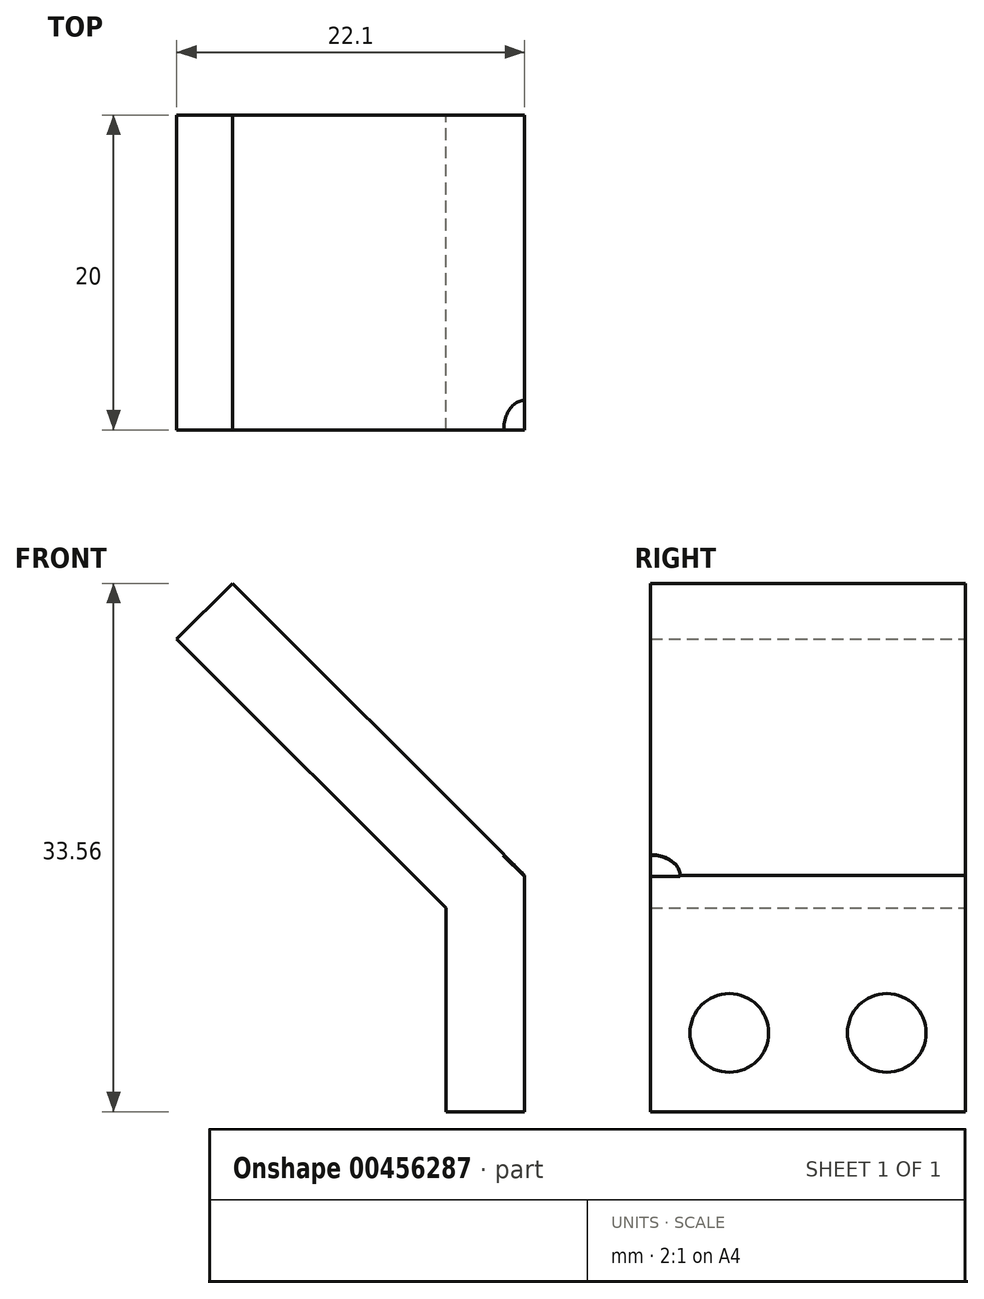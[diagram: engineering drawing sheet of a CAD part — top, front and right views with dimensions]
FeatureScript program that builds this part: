
annotation { "Feature Type Name" : "Feature", "Feature Type Description" : "" }
export const myFeature = defineFeature(function(context is Context, id is Id, definition is map)
    precondition{}
    {
        {
            var Q0;
            Q0=qCreatedBy(makeId("Front.planeOp"),FACE);
            var sketch = newSketch(context, id + "F0", { "sketchPlane" : qUnion([Q0])});
            skLineSegment(sketch, "E0", {"start": v(0, 0) * mm, "end": v(0, -15) * mm});
            skLineSegment(sketch, "E1", {"start": v(0, -15) * mm, "end": v(-5, -15) * mm});
            skLineSegment(sketch, "E2", {"start": v(-5, -15) * mm, "end": v(-5, -2.07) * mm});
            skLineSegment(sketch, "E3", {"start": v(-5, -2.07) * mm, "end": v(-22.1, 15.03) * mm});
            skLineSegment(sketch, "E4", {"start": v(-22.1, 15.03) * mm, "end": v(-18.56, 18.56) * mm});
            skLineSegment(sketch, "E5", {"start": v(-18.56, 18.56) * mm, "end": v(0, 0) * mm});
            skLineSegment(sketch, "E6", {"start": v(0, 0) * mm, "end": v(-5, -2.07) * mm});
            skSolve(sketch);
        }
        {
            var Q0;
            Q0 = qSketchRegion(id + "F0", true);
            extrude(context, id + "F1", {"entities" : qUnion([Q0]), "endBound" : BoundingType.SYMMETRIC, "depth" : 20 * mm, "offsetDistance" : 25 * mm});
        }
        {
            var Q0;
            Q0=makeQuery(id+"F1.opExtrude","SWEPT_FACE",FACE,{"disambiguationData":[OSD([sQuery(id+"F0.wireOp",EDGE,"E5")])]});
            var sketch = newSketch(context, id + "F2", { "sketchPlane" : qUnion([Q0])});
            skLineSegment(sketch, "E7", {"start": v(-26.25, 0) * mm, "end": v(-26.25, -6.25) * mm});
            skLineSegment(sketch, "E8", {"start": v(-26.25, 0) * mm, "end": v(-26.25, 6.25) * mm});
            skLineSegment(sketch, "E9", {"start": v(-26.25, 6.25) * mm, "end": v(0, 10) * mm});
            skLineSegment(sketch, "E10", {"start": v(0, -10) * mm, "end": v(-26.25, -6.25) * mm});
            skCircle(sketch, "E11", {"center": v(-20, 0) * mm, "radius": 1.88 * mm});
            skCircle(sketch, "E12", {"center": v(-10, 0) * mm, "radius": 1.88 * mm});
            skLineSegment(sketch, "E13", {"start": v(-20, -1.88) * mm, "end": v(-10, -1.88) * mm});
            skLineSegment(sketch, "E14", {"start": v(-20, 1.87) * mm, "end": v(-10, 1.87) * mm});
            skSolve(sketch);
        }
        {
            var Q0;
            Q0 = qSketchRegion(id + "F2", true);
            var Q1;
            {var subQ0=sQuery(id+"F2.wireOp",EDGE,"E9");Q1=makeQuery(id+"F2.imprint","IMPRINT",FACE,{"disambiguationData":[TD([[makeQuery(id+"F2.imprint","IMPRINT",EDGE,{"derivedFrom":subQ0}),1.0]])]});}
            var Q2;
            {var subQ0=sQuery(id+"F2.wireOp",EDGE,"E10");Q2=makeQuery(id+"F2.imprint","IMPRINT",FACE,{"disambiguationData":[TD([[makeQuery(id+"F2.imprint","IMPRINT",EDGE,{"derivedFrom":subQ0}),1.0]])]});}
            extrude(context, id + "F3", {"entities" : qUnion([Q0, Q1, Q2]), "operationType" : NewBodyOperationType.REMOVE, "oppositeDirection" : true, "depth" : 1 / 20 * mm, "offsetDistance" : 25 * mm});
        }
        {
            var Q0;
            Q0=qCreatedBy(makeId("Right.planeOp"),FACE);
            var sketch = newSketch(context, id + "F4", { "sketchPlane" : qUnion([Q0])});
            skCircle(sketch, "E15", {"center": v(-5, -10) * mm, "radius": 2.5 * mm});
            skCircle(sketch, "E16", {"center": v(5, -10) * mm, "radius": 2.5 * mm});
            skSolve(sketch);
        }
        {
            var Q0;
            Q0 = qSketchRegion(id + "F4", true);
            extrude(context, id + "F5", {"entities" : qUnion([Q0]), "operationType" : NewBodyOperationType.REMOVE, "oppositeDirection" : true, "depth" : 1 / 20 * mm, "offsetDistance" : 25 * mm});
        }
    });
